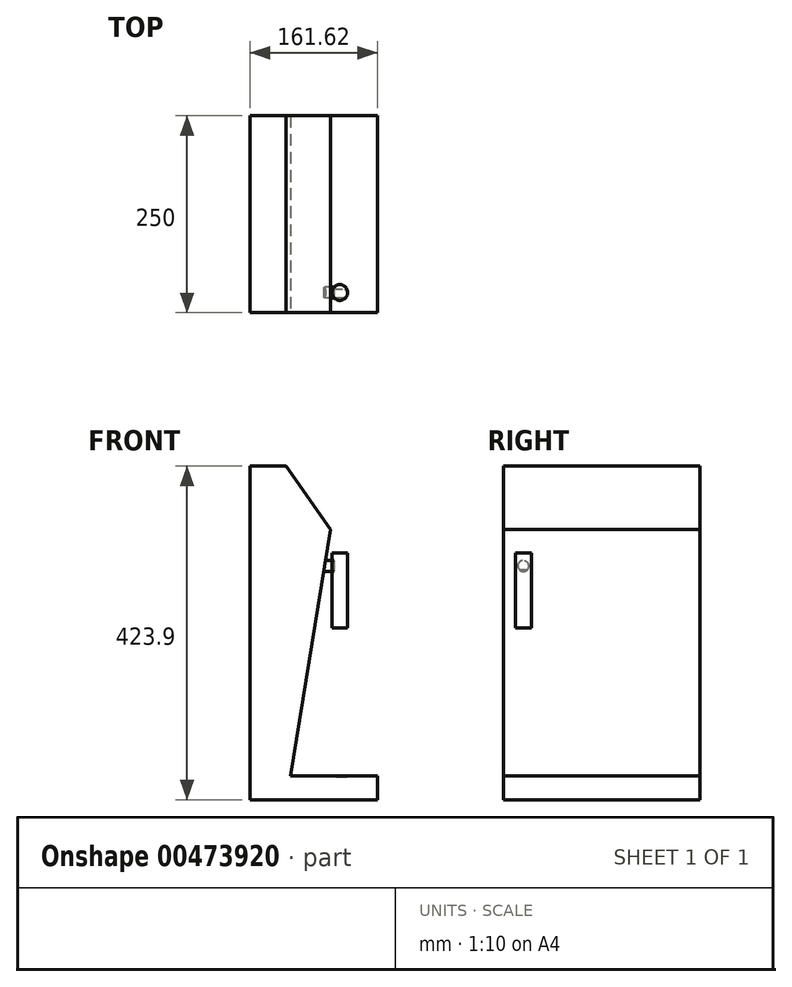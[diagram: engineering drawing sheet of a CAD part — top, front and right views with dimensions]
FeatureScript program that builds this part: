
annotation { "Feature Type Name" : "Feature", "Feature Type Description" : "" }
export const myFeature = defineFeature(function(context is Context, id is Id, definition is map)
    precondition{}
    {
        {
            var Q0;
            Q0=qCreatedBy(makeId("Front.planeOp"),FACE);
            var sketch = newSketch(context, id + "F0", { "sketchPlane" : qUnion([Q0])});
            skLineSegment(sketch, "E0", {"start": v(-80.84, -210.17) * mm, "end": v(-80.84, -240.17) * mm});
            skLineSegment(sketch, "E1", {"start": v(-80.84, -240.17) * mm, "end": v(80.78, -240.17) * mm});
            skLineSegment(sketch, "E2", {"start": v(80.78, -240.17) * mm, "end": v(80.78, -210.17) * mm});
            skLineSegment(sketch, "E3", {"start": v(80.78, -210.17) * mm, "end": v(-29.22, -210.17) * mm});
            skLineSegment(sketch, "E4", {"start": v(-29.22, -210.17) * mm, "end": v(21.26, 103.26) * mm});
            skLineSegment(sketch, "E5", {"start": v(21.26, 103.26) * mm, "end": v(-35.2, 183.73) * mm});
            skLineSegment(sketch, "E6", {"start": v(-35.2, 183.73) * mm, "end": v(-80.84, 183.73) * mm});
            skLineSegment(sketch, "E7", {"start": v(-80.84, 183.73) * mm, "end": v(-80.84, -210.17) * mm});
            skPoint(sketch, "E8", {"position": v(13.78, 56.83) * mm});
            skLineSegment(sketch, "E9", {"start": v(13.78, 56.83) * mm, "end": v(-80.84, 56.83) * mm, "construction": true});
            skLineSegment(sketch, "E10", {"start": v(-29.22, -210.17) * mm, "end": v(-29.22, 175.21) * mm, "construction": true});
            skSolve(sketch);
        }
        {
            var Q0;
            Q0=makeQuery(id+"F0.imprint","IMPRINT",FACE,{"disambiguationData":[TD([[makeQuery(id+"F0.imprint","IMPRINT",EDGE,{"derivedFrom":sQuery(id+"F0.wireOp",EDGE,"E0")}),1.0]])]});
            extrude(context, id + "F1", {"entities" : qUnion([Q0]), "oppositeDirection" : true, "depth" : 250 * mm});
        }
        {
            var Q0;
            Q0=makeQuery(id+"F1.opExtrude","SWEPT_FACE",FACE,{"disambiguationData":[OSD([sQuery(id+"F0.wireOp",EDGE,"E3")])]});
            var sketch = newSketch(context, id + "F2", { "sketchPlane" : qUnion([Q0])});
            skCircle(sketch, "E11", {"center": v(28.28, 24.5) * mm, "radius": 5.5 * mm});
            skCircle(sketch, "E12", {"center": v(36.78, 24.5) * mm, "radius": 5.5 * mm});
            skLineSegment(sketch, "E13", {"start": v(36.78, 24.5) * mm, "end": v(28.28, 24.5) * mm, "construction": true});
            skLineSegment(sketch, "E14", {"start": v(28.28, 24.5) * mm, "end": v(-29.22, 24.5) * mm, "construction": true});
            skPoint(sketch, "E15", {"position": v(22.78, 24.5) * mm});
            skPoint(sketch, "E16", {"position": v(42.28, 24.5) * mm});
            skLineSegment(sketch, "E17", {"start": v(28.28, 19) * mm, "end": v(36.78, 19) * mm});
            skLineSegment(sketch, "E18", {"start": v(28.28, 30) * mm, "end": v(36.78, 30) * mm});
            skSolve(sketch);
        }
        {
            var Q0;
            {var subQ0=sQuery(id+"F2.wireOp",EDGE,"E11");var subQ1=makeQuery(id+"F2.imprint","INTERSECT",VERTEX,{"derivedFrom":[subQ0,sQuery(id+"F2.wireOp",EDGE,"E18")]});Q0=makeQuery(id+"F2.imprint","IMPRINT",FACE,{"disambiguationData":[TD([[makeQuery(id+"F2.imprint","IMPRINT",EDGE,{"disambiguationData":[TD([[subQ1,1.0]])],"derivedFrom":subQ0}),1.0]])]});}
            var Q1;
            {var subQ0=sQuery(id+"F2.wireOp",EDGE,"E17");Q1=makeQuery(id+"F2.imprint","IMPRINT",FACE,{"disambiguationData":[TD([[makeQuery(id+"F2.imprint","IMPRINT",EDGE,{"derivedFrom":subQ0}),1.0]])]});}
            var Q2;
            {var subQ0=sQuery(id+"F2.wireOp",EDGE,"E12");var subQ1=sQuery(id+"F2.wireOp",EDGE,"E11");var subQ2=makeQuery(id+"F2.imprint","INTERSECT",VERTEX,{"disambiguationData":[OD(0.0)],"derivedFrom":[subQ1,subQ0]});Q2=makeQuery(id+"F2.imprint","IMPRINT",FACE,{"disambiguationData":[TD([[makeQuery(id+"F2.imprint","IMPRINT",EDGE,{"disambiguationData":[TD([[subQ2,1.0]])],"derivedFrom":subQ1}),1.0]])]});}
            var Q3;
            {var subQ0=sQuery(id+"F2.wireOp",EDGE,"E12");var subQ1=sQuery(id+"F2.wireOp",EDGE,"E11");var subQ2=makeQuery(id+"F2.imprint","INTERSECT",VERTEX,{"disambiguationData":[OD(0.0)],"derivedFrom":[subQ1,subQ0]});Q3=makeQuery(id+"F2.imprint","IMPRINT",FACE,{"disambiguationData":[TD([[makeQuery(id+"F2.imprint","IMPRINT",EDGE,{"disambiguationData":[TD([[subQ2,1.0]])],"derivedFrom":subQ1}),-1.0]])]});}
            var Q4;
            {var subQ0=sQuery(id+"F2.wireOp",EDGE,"E18");Q4=makeQuery(id+"F2.imprint","IMPRINT",FACE,{"disambiguationData":[TD([[makeQuery(id+"F2.imprint","IMPRINT",EDGE,{"derivedFrom":subQ0}),-1.0]])]});}
            extrude(context, id + "F3", {"entities" : qUnion([Q0, Q1, Q2, Q3, Q4]), "operationType" : NewBodyOperationType.REMOVE, "oppositeDirection" : true, "depth" : 1 * mm});
        }
        {
            var Q0;
            Q0=qCreatedBy(makeId("Right.planeOp"),FACE);
            var sketch = newSketch(context, id + "F4", { "sketchPlane" : qUnion([Q0])});
            skPoint(sketch, "E19.0", {"position": v(0, 56.83) * mm});
            skLineSegment(sketch, "E20", {"start": v(0, 56.83) * mm, "end": v(248.3, 56.83) * mm});
            skSolve(sketch);
        }
        {
            var Q0;
            Q0=sQuery(id+"F4.wireOp",EDGE,"E20");
            cPlane(context, id + "F5", {"entities" : qUnion([Q0]), "cplaneType" : CPlaneType.LINE_ANGLE, "offset" : 25 * mm, "angle" : 90 * degree, "width" : 150 * mm, "height" : 150 * mm});
        }
        {
            var Q0;
            Q0=qCreatedBy(id+"F5.planeOp",FACE);
            cPlane(context, id + "F6", {"entities" : qUnion([Q0]), "cplaneType" : CPlaneType.OFFSET, "offset" : 13 * mm, "width" : 150 * mm, "height" : 150 * mm});
        }
        {
            var Q0;
            Q0=qCreatedBy(id+"F6.planeOp",FACE);
            var sketch = newSketch(context, id + "F7", { "sketchPlane" : qUnion([Q0])});
            skCircle(sketch, "E21", {"center": v(25.5, 56.83) * mm, "radius": 7 * mm});
            skPoint(sketch, "E22.0", {"position": v(0, 56.83) * mm});
            skLineSegment(sketch, "E23", {"start": v(0, 56.83) * mm, "end": v(25.5, 56.83) * mm, "construction": true});
            skSolve(sketch);
        }
        {
            var Q0;
            Q0=makeQuery(id+"F7.imprint","IMPRINT",FACE,{"disambiguationData":[TD([[makeQuery(id+"F7.imprint","IMPRINT",EDGE,{"derivedFrom":sQuery(id+"F7.wireOp",EDGE,"E21")}),1.0]])]});
            extrude(context, id + "F8", {"entities" : qUnion([Q0]), "operationType" : NewBodyOperationType.ADD, "depth" : 13 * mm});
        }
        {
            var Q0;
            Q0=makeQuery(id+"F8.opExtrude","CAP_FACE",FACE,{"disambiguationData":[OSD([sQuery(id+"F7.wireOp",EDGE,"E21")])],"isStart":false});
            var sketch = newSketch(context, id + "F9", { "sketchPlane" : qUnion([Q0])});
            skLineSegment(sketch, "E24", {"start": v(18.5, 56.8) * mm, "end": v(32.5, 56.8) * mm});
            skSolve(sketch);
        }
        {
            var Q0;
            Q0=sQuery(id+"F9.wireOp",EDGE,"E24");
            cPlane(context, id + "F10", {"entities" : qUnion([Q0]), "cplaneType" : CPlaneType.LINE_ANGLE, "offset" : 25 * mm, "angle" : 0 * degree, "width" : 150 * mm, "height" : 150 * mm});
        }
        {
            var Q0;
            Q0=qCreatedBy(id+"F10.planeOp",FACE);
            var sketch = newSketch(context, id + "F11", { "sketchPlane" : qUnion([Q0])});
            skCircle(sketch, "E25", {"center": v(33.14, 25.5) * mm, "radius": 10 * mm});
            skLineSegment(sketch, "E26.0", {"start": v(26, 32.5) * mm, "end": v(26, 18.5) * mm});
            skSolve(sketch);
        }
        {
            var Q0;
            {var subQ0=sQuery(id+"F11.wireOp",EDGE,"E26.0");Q0=makeQuery(id+"F11.imprint","IMPRINT",FACE,{"disambiguationData":[TD([[makeQuery(id+"F11.imprint","IMPRINT",EDGE,{"derivedFrom":subQ0}),1.0]])]});}
            var Q1;
            {var subQ0=sQuery(id+"F11.wireOp",EDGE,"E26.0");Q1=makeQuery(id+"F11.imprint","IMPRINT",FACE,{"disambiguationData":[TD([[makeQuery(id+"F11.imprint","IMPRINT",EDGE,{"derivedFrom":subQ0}),-1.0]])]});}
            extrude(context, id + "F12", {"entities" : qUnion([Q0, Q1]), "oppositeDirection" : true, "depth" : 95 * mm});
        }
        {
            var Q0;
            Q0=makeQuery(id+"F12.opExtrude","SWEPT_BODY",BODY,{"disambiguationData":[OSD([sQuery(id+"F11.wireOp",EDGE,"E25"),sQuery(id+"F11.wireOp",EDGE,"E26.0")])]});
            transform(context, id + "F13", {"entities" : qUnion([Q0]), "transformType" : TransformType.TRANSLATION_3D, "dx" : 0 * mm, "dy" : 0 * mm, "dz" : 16.3 * mm, "makeCopy" : false});
        }
    });
